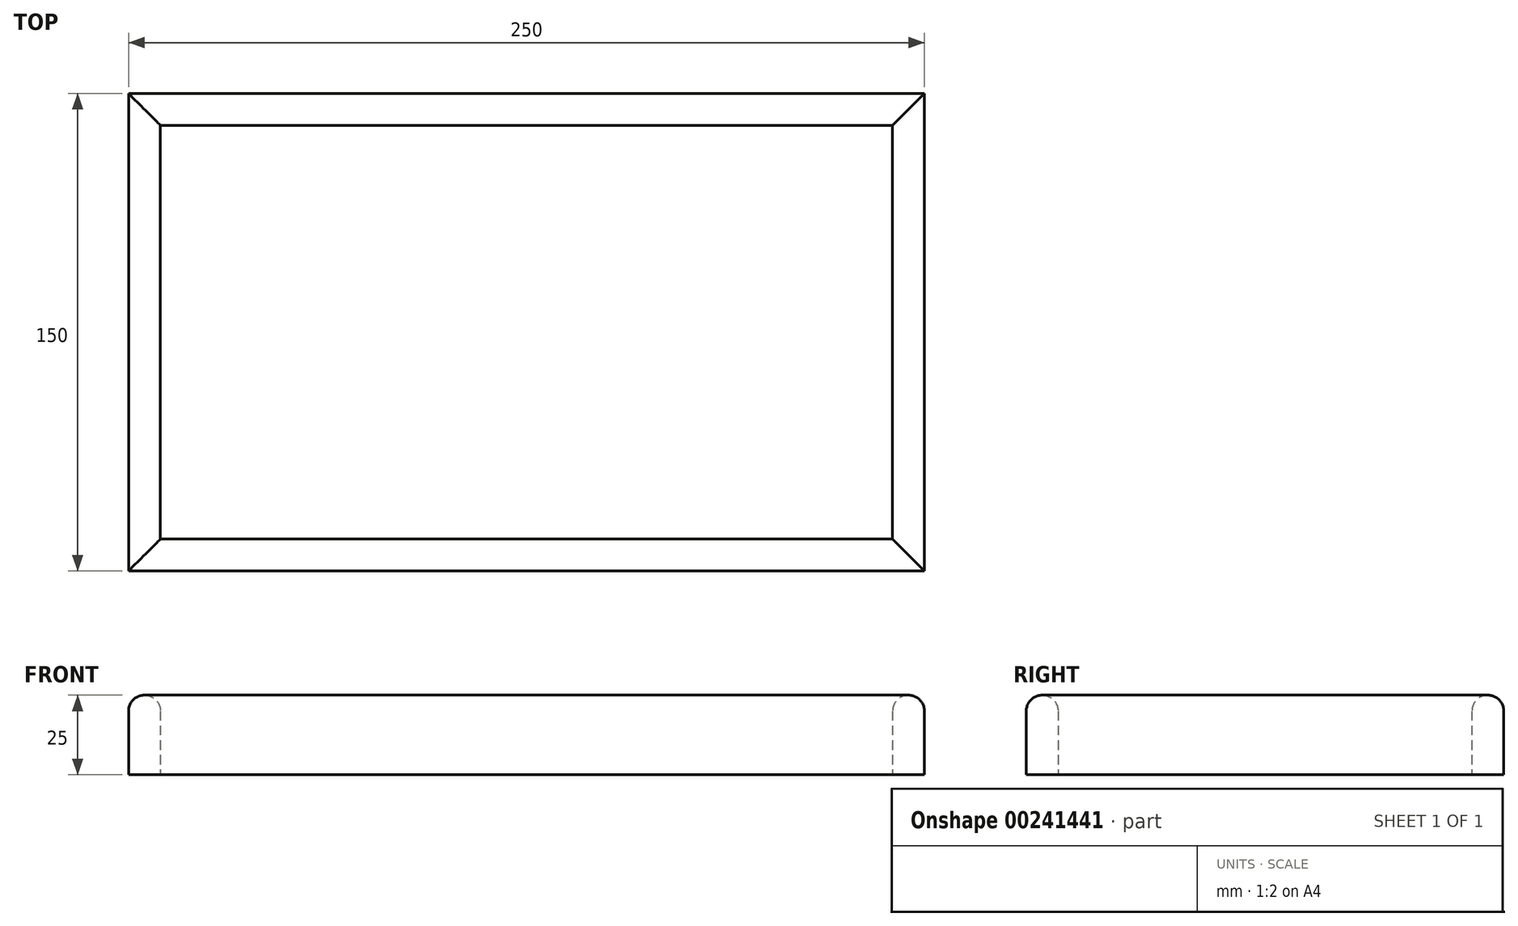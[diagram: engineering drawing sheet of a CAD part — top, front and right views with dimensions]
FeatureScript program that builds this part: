
annotation { "Feature Type Name" : "Feature", "Feature Type Description" : "" }
export const myFeature = defineFeature(function(context is Context, id is Id, definition is map)
    precondition{}
    {
        {
            var Q0;
            Q0=qCreatedBy(makeId("Top.planeOp"),FACE);
            var sketch = newSketch(context, id + "F0", { "sketchPlane" : qUnion([Q0])});
            skLineSegment(sketch, "E0.bottom", {"start": v(-125, 75) * mm, "end": v(125, 75) * mm});
            skLineSegment(sketch, "E0.top", {"start": v(-125, -75) * mm, "end": v(125, -75) * mm});
            skLineSegment(sketch, "E0.left", {"start": v(-125, 75) * mm, "end": v(-125, -75) * mm});
            skLineSegment(sketch, "E0.right", {"start": v(125, 75) * mm, "end": v(125, -75) * mm});
            skPoint(sketch, "E0.middle", {"position": v(0, 0) * mm});
            skLineSegment(sketch, "E1.bottom", {"start": v(-115, 65) * mm, "end": v(115, 65) * mm});
            skLineSegment(sketch, "E1.top", {"start": v(-115, -65) * mm, "end": v(115, -65) * mm});
            skLineSegment(sketch, "E1.left", {"start": v(-115, 65) * mm, "end": v(-115, -65) * mm});
            skLineSegment(sketch, "E1.right", {"start": v(115, 65) * mm, "end": v(115, -65) * mm});
            skSolve(sketch);
        }
        {
            var Q0;
            Q0 = qSketchRegion(id + "F0", true);
            extrude(context, id + "F1", {"entities" : qUnion([Q0]), "depth" : 25 * mm});
        }
        {
            var Q0;
            Q0=makeQuery(id+"F1.opExtrude","CAP_FACE",FACE,{"disambiguationData":[OSD([sQuery(id+"F0.wireOp",EDGE,"E0.bottom"),sQuery(id+"F0.wireOp",EDGE,"E0.top"),sQuery(id+"F0.wireOp",EDGE,"E0.left"),sQuery(id+"F0.wireOp",EDGE,"E0.right"),sQuery(id+"F0.wireOp",EDGE,"E1.bottom"),sQuery(id+"F0.wireOp",EDGE,"E1.top"),sQuery(id+"F0.wireOp",EDGE,"E1.left"),sQuery(id+"F0.wireOp",EDGE,"E1.right")])],"isStart":false});
            fillet(context, id + "F2", {"entities" : qUnion([Q0]), "radius" : 5 * mm, "tangentPropagation" : true, "allowEdgeOverflow" : false});
        }
    });
